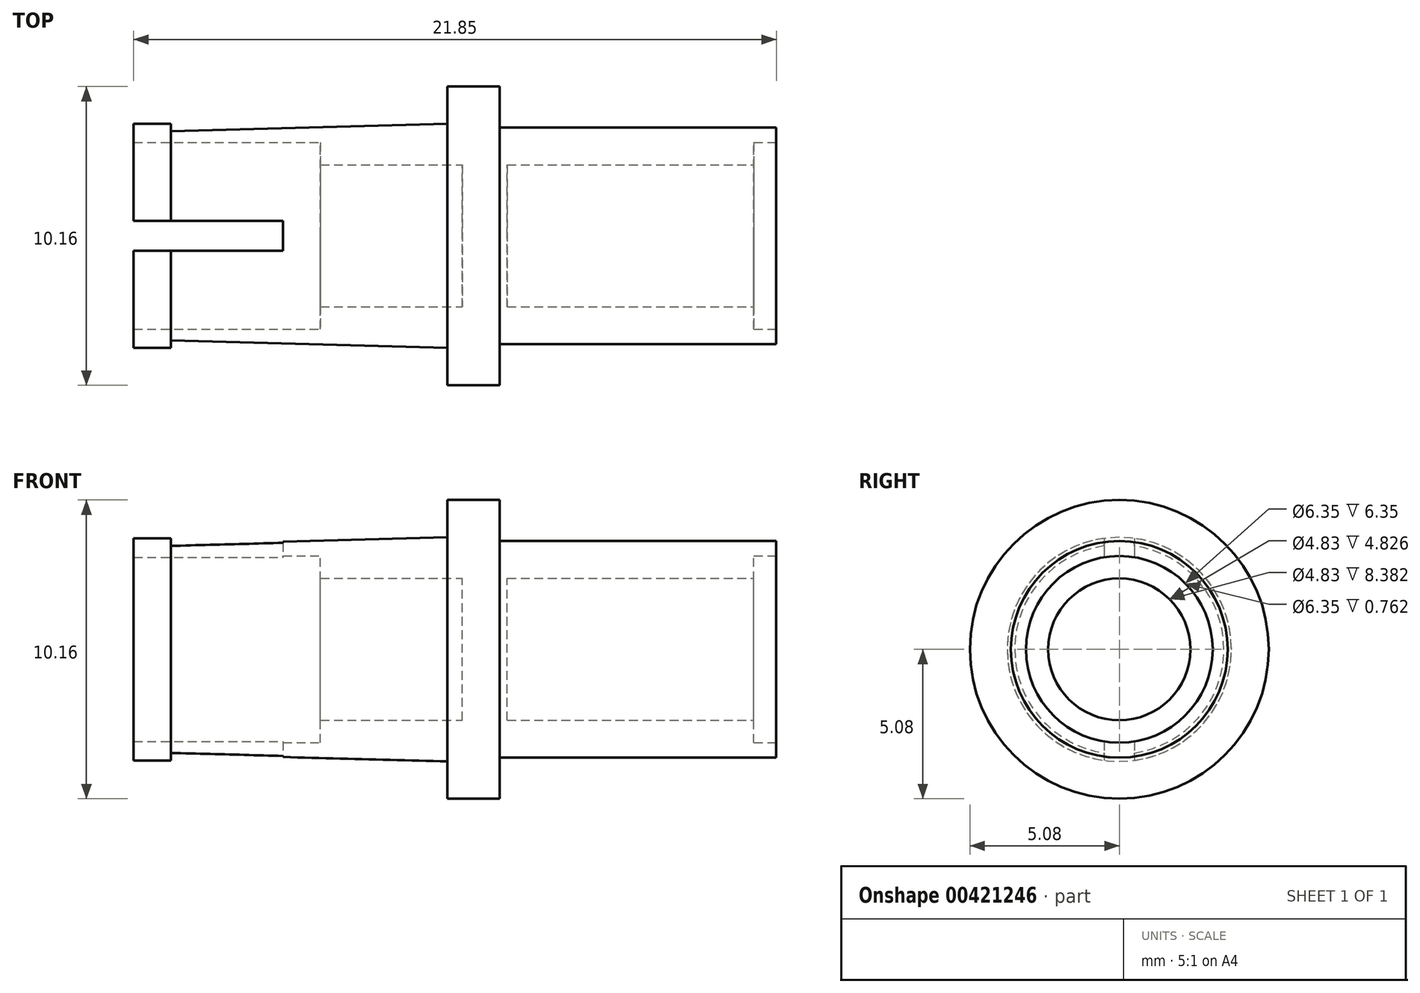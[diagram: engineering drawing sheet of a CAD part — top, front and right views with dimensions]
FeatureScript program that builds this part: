
annotation { "Feature Type Name" : "Feature", "Feature Type Description" : "" }
export const myFeature = defineFeature(function(context is Context, id is Id, definition is map)
    precondition{}
    {
        {
            var Q0;
            Q0=qCreatedBy(makeId("Front.planeOp"),FACE);
            var sketch = newSketch(context, id + "F0", { "sketchPlane" : qUnion([Q0])});
            skLineSegment(sketch, "E0", {"start": v(0, 0) * mm, "end": v(0, 1.27) * mm});
            skLineSegment(sketch, "E1", {"start": v(0, 1.27) * mm, "end": v(1.78, 1.27) * mm});
            skLineSegment(sketch, "E2", {"start": v(1.78, 1.27) * mm, "end": v(1.78, -0.13) * mm});
            skLineSegment(sketch, "E3", {"start": v(1.78, -0.13) * mm, "end": v(11.18, -0.13) * mm});
            skLineSegment(sketch, "E4", {"start": v(11.18, -0.13) * mm, "end": v(11.18, -0.63) * mm});
            skLineSegment(sketch, "E5", {"start": v(11.18, -0.63) * mm, "end": v(10.41, -0.63) * mm});
            skLineSegment(sketch, "E6", {"start": v(10.41, -0.63) * mm, "end": v(10.41, -1.4) * mm});
            skLineSegment(sketch, "E7", {"start": v(10.41, -1.4) * mm, "end": v(2.03, -1.4) * mm});
            skLineSegment(sketch, "E8", {"start": v(2.03, -1.4) * mm, "end": v(2.03, -3.81) * mm});
            skLineSegment(sketch, "E9", {"start": v(2.03, -3.81) * mm, "end": v(0.5, -3.81) * mm});
            skLineSegment(sketch, "E10", {"start": v(0.5, -3.81) * mm, "end": v(0.5, -1.4) * mm});
            skLineSegment(sketch, "E11", {"start": v(0.5, -1.4) * mm, "end": v(-4.32, -1.4) * mm});
            skLineSegment(sketch, "E12", {"start": v(-4.32, -1.4) * mm, "end": v(-4.32, -0.64) * mm});
            skLineSegment(sketch, "E13", {"start": v(-4.32, -0.64) * mm, "end": v(-10.67, -0.64) * mm});
            skLineSegment(sketch, "E14", {"start": v(-10.67, -0.64) * mm, "end": v(-10.67, 0) * mm});
            skLineSegment(sketch, "E15", {"start": v(-10.67, 0) * mm, "end": v(-9.4, 0) * mm});
            skLineSegment(sketch, "E16", {"start": v(-9.4, 0) * mm, "end": v(-9.4, -0.25) * mm});
            skLineSegment(sketch, "E17", {"start": v(-9.4, -0.25) * mm, "end": v(0, 0) * mm});
            skSolve(sketch);
        }
        {
            var Q0;
            Q0=makeQuery(id+"F0.imprint","IMPRINT",FACE,{"disambiguationData":[TD([[makeQuery(id+"F0.imprint","IMPRINT",EDGE,{"derivedFrom":sQuery(id+"F0.wireOp",EDGE,"E0")}),-1.0]])]});
            var Q1;
            Q1=sQuery(id+"F0.wireOp",EDGE,"E9");
            revolve(context, id + "F1", {"entities" : qUnion([Q0]), "axis" : qUnion([Q1]), "revolveType" : RevolveType.FULL});
        }
        {
            var Q0;
            Q0=makeQuery(id+"F1.opRevolve","SWEPT_FACE",FACE,{"disambiguationData":[OSD([sQuery(id+"F0.wireOp",EDGE,"E14")])]});
            var sketch = newSketch(context, id + "F2", { "sketchPlane" : qUnion([Q0])});
            skLineSegment(sketch, "E18.bottom", {"start": v(-0.5, 380996.19) * mm, "end": v(0.5, 380996.19) * mm});
            skLineSegment(sketch, "E18.top", {"start": v(-0.5, -381003.81) * mm, "end": v(0.5, -381003.81) * mm});
            skLineSegment(sketch, "E18.left", {"start": v(-0.5, 380996.19) * mm, "end": v(-0.5, -381003.81) * mm});
            skLineSegment(sketch, "E18.right", {"start": v(0.5, 380996.19) * mm, "end": v(0.5, -381003.81) * mm});
            skPoint(sketch, "E18.middle", {"position": v(0, -3.81) * mm});
            skSolve(sketch);
        }
        {
            var Q0;
            {var subQ0=sQuery(id+"F2.wireOp",EDGE,"E18.left");var subQ1=makeQuery(id+"F1.opRevolve","SWEPT_EDGE",EDGE,{"disambiguationData":[OSD([sQuery(id+"F0.wireOp",EDGE,"E13"),sQuery(id+"F0.wireOp",EDGE,"E14")])]});var subQ2=makeQuery(id+"F2.imprint","INTERSECT",VERTEX,{"disambiguationData":[OD(0.0)],"derivedFrom":[subQ1,subQ0]});Q0=makeQuery(id+"F2.imprint","IMPRINT",FACE,{"disambiguationData":[TD([[makeQuery(id+"F2.imprint","IMPRINT",EDGE,{"disambiguationData":[TD([[subQ2,-1.0]])],"derivedFrom":subQ0}),1.0]])]});}
            var Q1;
            {var subQ0=sQuery(id+"F2.wireOp",EDGE,"E18.left");var subQ1=sQuery(id+"F0.wireOp",EDGE,"E14");var subQ2=makeQuery(id+"F1.opRevolve","SWEPT_EDGE",EDGE,{"disambiguationData":[OSD([subQ1,sQuery(id+"F0.wireOp",EDGE,"E15")])]});var subQ3=makeQuery(id+"F2.imprint","INTERSECT",VERTEX,{"disambiguationData":[OD(0.0)],"derivedFrom":[subQ2,subQ0]});Q1=makeQuery(id+"F2.imprint","IMPRINT",FACE,{"disambiguationData":[TD([[makeQuery(id+"F2.imprint","IMPRINT",EDGE,{"disambiguationData":[TD([[subQ3,-1.0]])],"derivedFrom":subQ0}),1.0]])]});}
            var Q2;
            {var subQ0=sQuery(id+"F2.wireOp",EDGE,"E18.left");var subQ1=sQuery(id+"F0.wireOp",EDGE,"E14");var subQ2=makeQuery(id+"F1.opRevolve","SWEPT_EDGE",EDGE,{"disambiguationData":[OSD([subQ1,sQuery(id+"F0.wireOp",EDGE,"E15")])]});var subQ3=makeQuery(id+"F2.imprint","INTERSECT",VERTEX,{"disambiguationData":[OD(1.0)],"derivedFrom":[subQ2,subQ0]});Q2=makeQuery(id+"F2.imprint","IMPRINT",FACE,{"disambiguationData":[TD([[makeQuery(id+"F2.imprint","IMPRINT",EDGE,{"disambiguationData":[TD([[subQ3,1.0]])],"derivedFrom":subQ0}),1.0]])]});}
            var Q3;
            {var subQ0=sQuery(id+"F2.wireOp",EDGE,"E18.top");Q3=makeQuery(id+"F2.imprint","IMPRINT",FACE,{"disambiguationData":[TD([[makeQuery(id+"F2.imprint","IMPRINT",EDGE,{"derivedFrom":subQ0}),1.0]])]});}
            var Q4;
            {var subQ0=sQuery(id+"F2.wireOp",EDGE,"E18.bottom");Q4=makeQuery(id+"F2.imprint","IMPRINT",FACE,{"disambiguationData":[TD([[makeQuery(id+"F2.imprint","IMPRINT",EDGE,{"derivedFrom":subQ0}),-1.0]])]});}
            extrude(context, id + "F3", {"entities" : qUnion([Q0, Q1, Q2, Q3, Q4]), "operationType" : NewBodyOperationType.REMOVE, "oppositeDirection" : true, "depth" : 5.08 * mm});
        }
    });
